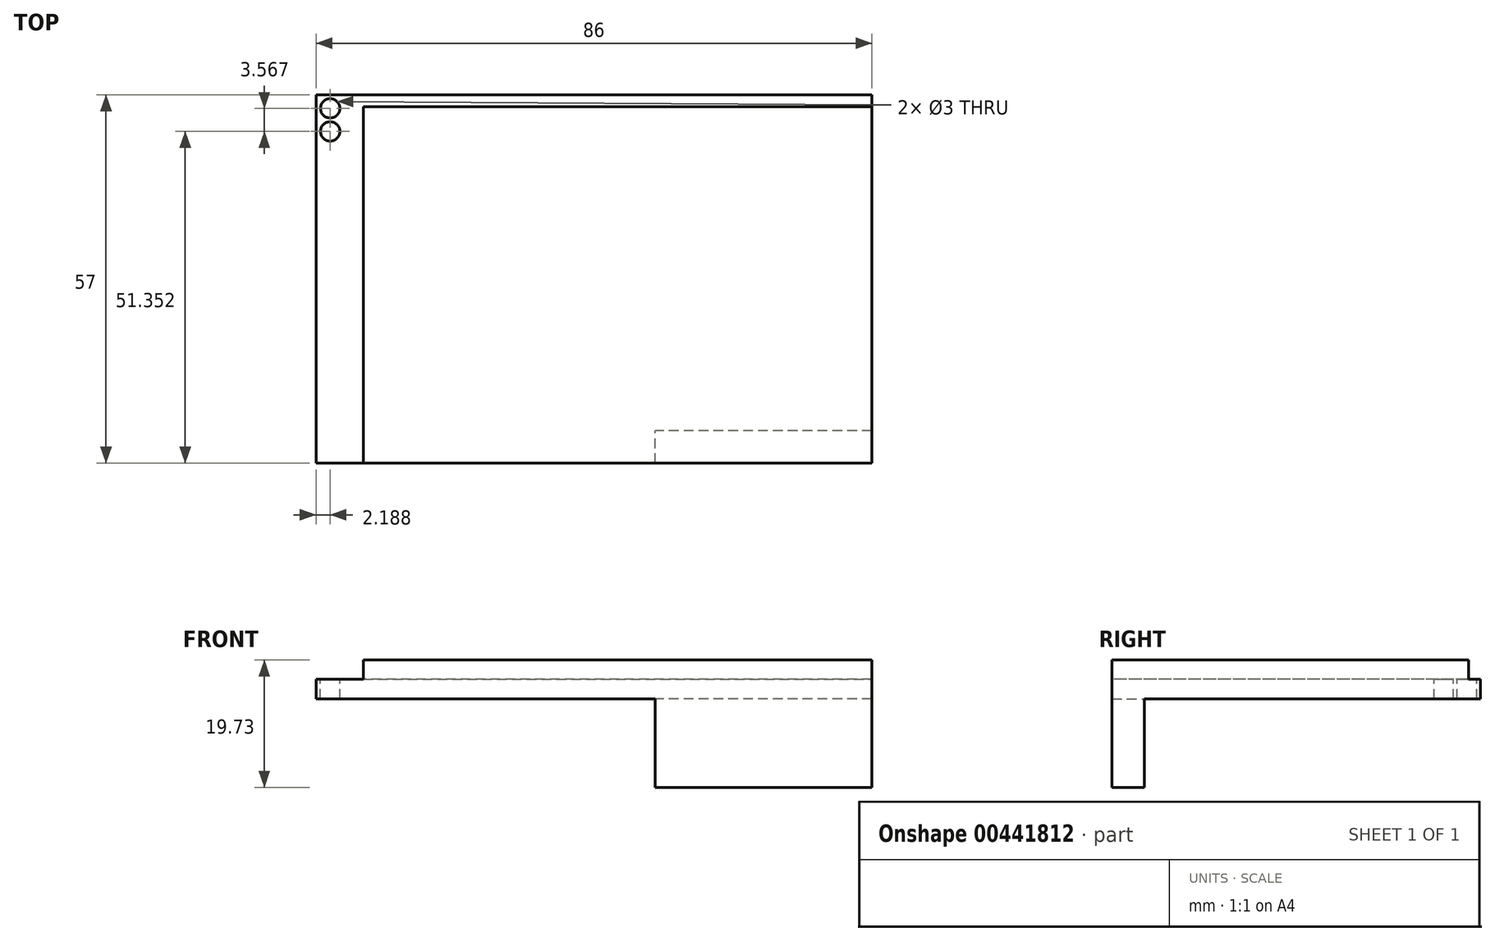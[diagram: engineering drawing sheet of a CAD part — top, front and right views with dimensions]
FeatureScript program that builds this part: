
annotation { "Feature Type Name" : "Feature", "Feature Type Description" : "" }
export const myFeature = defineFeature(function(context is Context, id is Id, definition is map)
    precondition{}
    {
        {
            var Q0;
            Q0=qCreatedBy(makeId("Top.planeOp"),FACE);
            var sketch = newSketch(context, id + "F0", { "sketchPlane" : qUnion([Q0])});
            skLineSegment(sketch, "E0.bottom", {"start": v(43, 28.5) * mm, "end": v(-43, 28.5) * mm});
            skLineSegment(sketch, "E0.top", {"start": v(43, -28.5) * mm, "end": v(-43, -28.5) * mm});
            skLineSegment(sketch, "E0.left", {"start": v(43, 28.5) * mm, "end": v(43, -28.5) * mm});
            skLineSegment(sketch, "E0.right", {"start": v(-43, 28.5) * mm, "end": v(-43, -28.5) * mm});
            skPoint(sketch, "E0.middle", {"position": v(0, 0) * mm});
            skSolve(sketch);
        }
        {
            var Q0;
            Q0 = qSketchRegion(id + "F0", true);
            extrude(context, id + "F1", {"entities" : qUnion([Q0]), "depth" : 3 * mm});
        }
        {
            var Q0;
            Q0=makeQuery(id+"F1.opExtrude","CAP_FACE",FACE,{"disambiguationData":[OSD([sQuery(id+"F0.wireOp",EDGE,"E0.bottom"),sQuery(id+"F0.wireOp",EDGE,"E0.top"),sQuery(id+"F0.wireOp",EDGE,"E0.left"),sQuery(id+"F0.wireOp",EDGE,"E0.right")])],"isStart":false});
            var sketch = newSketch(context, id + "F2", { "sketchPlane" : qUnion([Q0])});
            skLineSegment(sketch, "E1.bottom", {"start": v(-35.7, 26.7) * mm, "end": v(43, 26.7) * mm});
            skLineSegment(sketch, "E1.top", {"start": v(-35.7, -28.5) * mm, "end": v(43, -28.5) * mm});
            skLineSegment(sketch, "E1.left", {"start": v(-35.7, 26.7) * mm, "end": v(-35.7, -28.5) * mm});
            skLineSegment(sketch, "E1.right", {"start": v(43, 26.7) * mm, "end": v(43, -28.5) * mm});
            skSolve(sketch);
        }
        {
            var Q0;
            Q0 = qSketchRegion(id + "F2", true);
            extrude(context, id + "F3", {"entities" : qUnion([Q0]), "operationType" : NewBodyOperationType.ADD, "depth" : 3 * mm});
        }
        {
            var Q0;
            Q0=makeQuery(id+"F1.opExtrude","CAP_FACE",FACE,{"disambiguationData":[OSD([sQuery(id+"F0.wireOp",EDGE,"E0.bottom"),sQuery(id+"F0.wireOp",EDGE,"E0.top"),sQuery(id+"F0.wireOp",EDGE,"E0.left"),sQuery(id+"F0.wireOp",EDGE,"E0.right")])],"isStart":false});
            var sketch = newSketch(context, id + "F4", { "sketchPlane" : qUnion([Q0])});
            skCircle(sketch, "E2", {"center": v(-40.81, 26.42) * mm, "radius": 1.5 * mm});
            skCircle(sketch, "E3", {"center": v(-40.81, 22.85) * mm, "radius": 1.5 * mm});
            skSolve(sketch);
        }
        {
            var Q0;
            Q0 = qSketchRegion(id + "F4", true);
            extrude(context, id + "F5", {"entities" : qUnion([Q0]), "operationType" : NewBodyOperationType.REMOVE, "oppositeDirection" : true, "depth" : 25 * mm});
        }
        {
            var Q0;
            Q0=makeQuery(id+"F1.opExtrude","CAP_FACE",FACE,{"disambiguationData":[OSD([sQuery(id+"F0.wireOp",EDGE,"E0.bottom"),sQuery(id+"F0.wireOp",EDGE,"E0.top"),sQuery(id+"F0.wireOp",EDGE,"E0.left"),sQuery(id+"F0.wireOp",EDGE,"E0.right")])],"isStart":true});
            var sketch = newSketch(context, id + "F6", { "sketchPlane" : qUnion([Q0])});
            skLineSegment(sketch, "E4.bottom", {"start": v(43, 28.5) * mm, "end": v(9.5, 28.5) * mm});
            skLineSegment(sketch, "E4.top", {"start": v(43, 23.5) * mm, "end": v(9.5, 23.5) * mm});
            skLineSegment(sketch, "E4.left", {"start": v(43, 28.5) * mm, "end": v(43, 23.5) * mm});
            skLineSegment(sketch, "E4.right", {"start": v(9.5, 28.5) * mm, "end": v(9.5, 23.5) * mm});
            skSolve(sketch);
        }
        {
            var Q0;
            Q0 = qSketchRegion(id + "F6", true);
            extrude(context, id + "F7", {"entities" : qUnion([Q0]), "operationType" : NewBodyOperationType.ADD, "depth" : 13.73 * mm});
        }
    });
